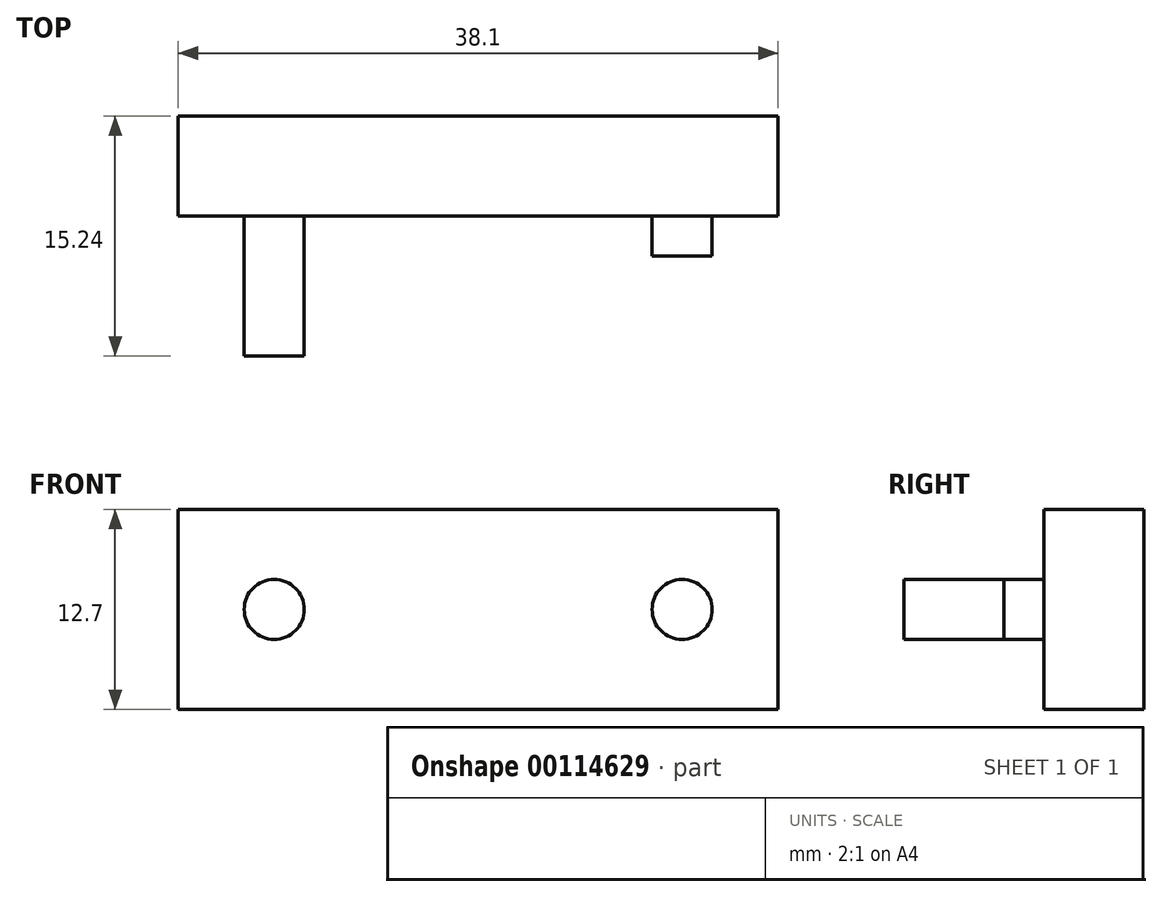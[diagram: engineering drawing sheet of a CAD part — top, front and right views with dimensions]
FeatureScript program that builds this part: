
annotation { "Feature Type Name" : "Feature", "Feature Type Description" : "" }
export const myFeature = defineFeature(function(context is Context, id is Id, definition is map)
    precondition{}
    {
        {
            var Q0;
            Q0=qCreatedBy(makeId("Front.planeOp"),FACE);
            var sketch = newSketch(context, id + "F0", { "sketchPlane" : qUnion([Q0])});
            skLineSegment(sketch, "E0.bottom", {"start": v(19.05, -6.35) * mm, "end": v(-19.05, -6.35) * mm});
            skLineSegment(sketch, "E0.top", {"start": v(19.05, 6.35) * mm, "end": v(-19.05, 6.35) * mm});
            skLineSegment(sketch, "E0.left", {"start": v(19.05, -6.35) * mm, "end": v(19.05, 6.35) * mm});
            skLineSegment(sketch, "E0.right", {"start": v(-19.05, -6.35) * mm, "end": v(-19.05, 6.35) * mm});
            skPoint(sketch, "E0.middle", {"position": v(0, 0) * mm});
            skSolve(sketch);
        }
        {
            var Q0;
            Q0 = qSketchRegion(id + "F0", true);
            extrude(context, id + "F1", {"entities" : qUnion([Q0]), "depth" : 6.35 * mm});
        }
        {
            var Q0;
            Q0=makeQuery(id+"F1.opExtrude","CAP_FACE",FACE,{"disambiguationData":[OSD([sQuery(id+"F0.wireOp",EDGE,"E0.bottom"),sQuery(id+"F0.wireOp",EDGE,"E0.top"),sQuery(id+"F0.wireOp",EDGE,"E0.left"),sQuery(id+"F0.wireOp",EDGE,"E0.right")])],"isStart":false});
            var sketch = newSketch(context, id + "F2", { "sketchPlane" : qUnion([Q0])});
            skLineSegment(sketch, "E1", {"start": v(0, 0) * mm, "end": v(-12.95, 0) * mm, "construction": true});
            skCircle(sketch, "E2", {"center": v(-12.95, 0) * mm, "radius": 1.9 * mm});
            skSolve(sketch);
        }
        {
            var Q0;
            Q0 = qSketchRegion(id + "F2", true);
            extrude(context, id + "F3", {"entities" : qUnion([Q0]), "operationType" : NewBodyOperationType.ADD, "depth" : 8.9 * mm});
        }
        {
            var Q0;
            Q0=makeQuery(id+"F1.opExtrude","CAP_FACE",FACE,{"disambiguationData":[OSD([sQuery(id+"F0.wireOp",EDGE,"E0.bottom"),sQuery(id+"F0.wireOp",EDGE,"E0.top"),sQuery(id+"F0.wireOp",EDGE,"E0.left"),sQuery(id+"F0.wireOp",EDGE,"E0.right")])],"isStart":false});
            var sketch = newSketch(context, id + "F4", { "sketchPlane" : qUnion([Q0])});
            skLineSegment(sketch, "E3", {"start": v(0, 0) * mm, "end": v(12.95, 0) * mm, "construction": true});
            skCircle(sketch, "E4", {"center": v(12.95, 0) * mm, "radius": 1.9 * mm});
            skSolve(sketch);
        }
        {
            var Q0;
            Q0 = qSketchRegion(id + "F4", true);
            extrude(context, id + "F5", {"entities" : qUnion([Q0]), "operationType" : NewBodyOperationType.ADD, "depth" : 2.54 * mm});
        }
    });
